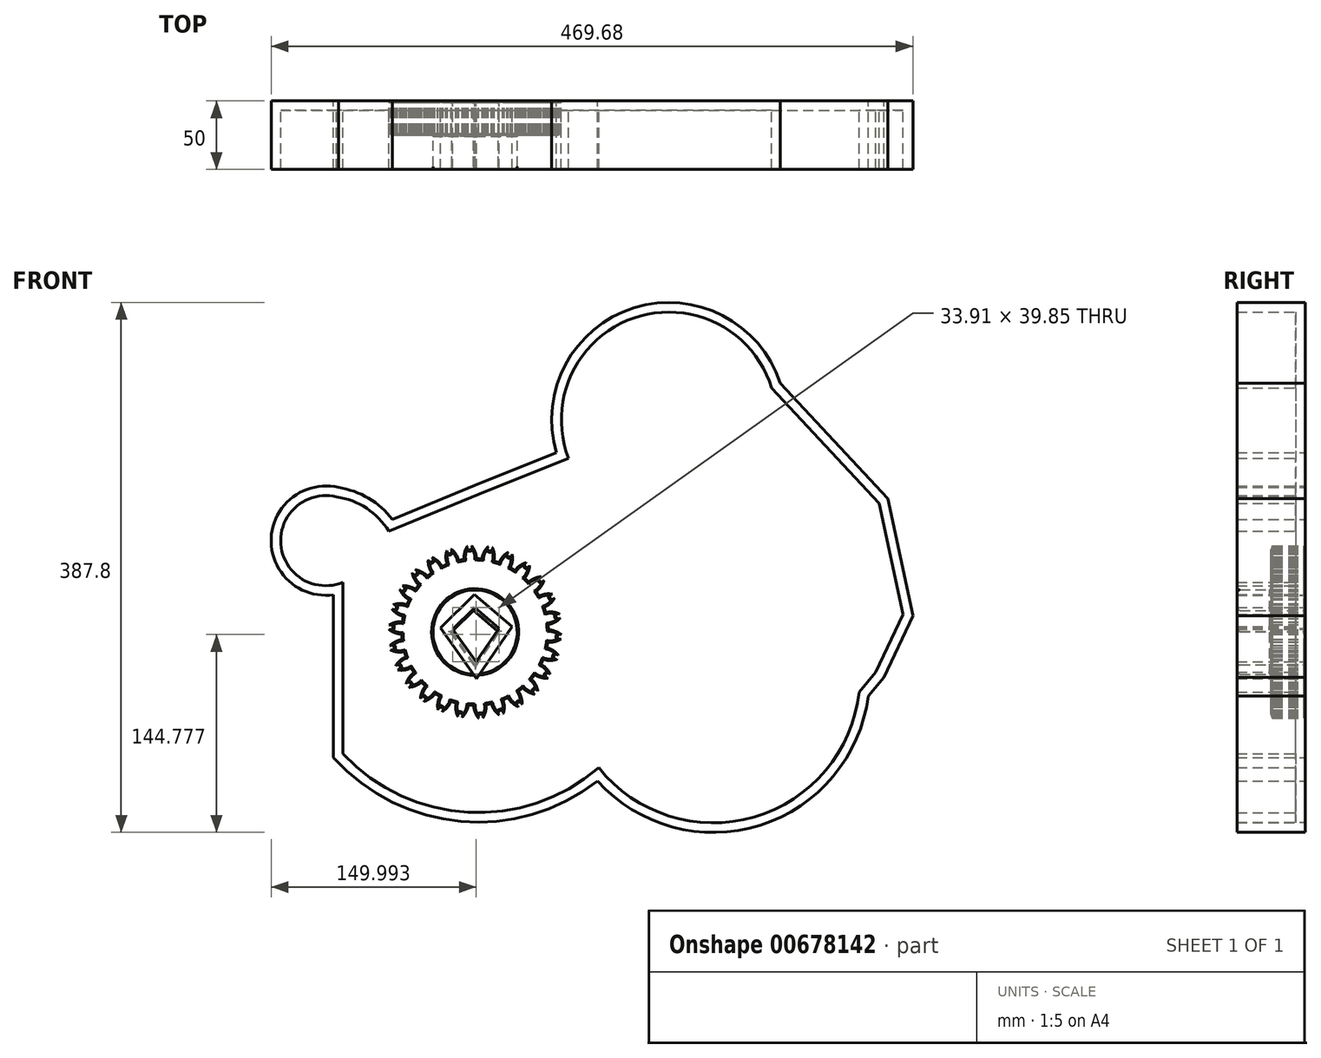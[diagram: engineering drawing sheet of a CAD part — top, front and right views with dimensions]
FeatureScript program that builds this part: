
annotation { "Feature Type Name" : "Feature", "Feature Type Description" : "" }
export const myFeature = defineFeature(function(context is Context, id is Id, definition is map)
    precondition{}
    {
        {
            var Q0;
            Q0=qCreatedBy(makeId("Front.planeOp"),FACE);
            var sketch = newSketch(context, id + "F0", { "sketchPlane" : qUnion([Q0])});
            skCircle(sketch, "E0", {"center": v(0, 0) * mm, "radius": 53.72 * mm});
            skCircle(sketch, "E1", {"center": v(0, 0) * mm, "radius": 58.67 * mm, "construction": true});
            skCircle(sketch, "E2", {"center": v(0, 0) * mm, "radius": 63.5 * mm, "construction": true});
            skLineSegment(sketch, "E3", {"start": v(0, 0) * mm, "end": v(0, 86.26) * mm, "construction": true});
            skLineSegment(sketch, "E4", {"start": v(0, 0) * mm, "end": v(-5.65, 86.26) * mm, "construction": true});
            skLineSegment(sketch, "E5", {"start": v(0, 58.67) * mm, "end": v(-58.15, 58.67) * mm, "construction": true});
            skLineSegment(sketch, "E6", {"start": v(0, 58.67) * mm, "end": v(-58.26, 37.47) * mm, "construction": true});
            skCircle(sketch, "E7", {"center": v(0, 0) * mm, "radius": 55.14 * mm, "construction": true});
            skCircle(sketch, "E8", {"center": v(0, 58.67) * mm, "radius": 14.6 * mm, "construction": true});
            skCircle(sketch, "E9", {"center": v(-13.72, 53.68) * mm, "radius": 14.6 * mm, "construction": true});
            skArc(sketch, "E10", {"start": v(0, 58.67) * mm, "mid": v(-1.18, 61.2) * mm, "end": v(-2.86, 63.44) * mm});
            skArc(sketch, "E11", {"start": v(0.88, 53.71) * mm, "mid": v(0.7, 56.24) * mm, "end": v(0, 58.67) * mm});
            skArc(sketch, "E12.MirrorCS", {"start": v(-7.66, 58.17) * mm, "mid": v(-6.82, 60.83) * mm, "end": v(-5.45, 63.27) * mm});
            skArc(sketch, "E13.MirrorCS", {"start": v(-7.88, 53.14) * mm, "mid": v(-8.04, 55.67) * mm, "end": v(-7.66, 58.17) * mm});
            skArc(sketch, "E14", {"start": v(-5.45, 63.27) * mm, "mid": v(-3.94, 60.17) * mm, "end": v(-2.86, 63.44) * mm});
            skCircle(sketch, "E15", {"center": v(0, 0) * mm, "radius": 30.81 * mm});
            skLineSegment(sketch, "E16", {"start": v(0, -24) * mm, "end": v(-17.1, 0) * mm});
            skLineSegment(sketch, "E17", {"start": v(-17.1, 0) * mm, "end": v(-1.04, 15.85) * mm});
            skLineSegment(sketch, "E18", {"start": v(-1.04, 15.85) * mm, "end": v(16.81, 0.43) * mm});
            skLineSegment(sketch, "E19", {"start": v(16.81, 0.43) * mm, "end": v(0, -24) * mm});
            skCircle(sketch, "E20", {"center": v(121.02, 0) * mm, "radius": 6 * mm});
            skSolve(sketch);
        }
        {
            var Q0;
            {var subQ0=sQuery(id+"F0.wireOp",EDGE,"E0");var subQ1=makeQuery(id+"F0.imprint","INTERSECT",VERTEX,{"derivedFrom":[subQ0,sQuery(id+"F0.wireOp",EDGE,"E11")]});Q0=makeQuery(id+"F0.imprint","IMPRINT",FACE,{"disambiguationData":[TD([[makeQuery(id+"F0.imprint","IMPRINT",EDGE,{"disambiguationData":[TD([[subQ1,-1.0]])],"derivedFrom":subQ0}),1.0]])]});}
            var Q1;
            {var subQ0=sQuery(id+"F0.wireOp",EDGE,"E11");Q1=makeQuery(id+"F0.imprint","IMPRINT",FACE,{"disambiguationData":[TD([[makeQuery(id+"F0.imprint","IMPRINT",EDGE,{"derivedFrom":subQ0}),1.0]])]});}
            extrude(context, id + "F1", {"entities" : qUnion([Q0, Q1]), "depth" : 25 * mm, "offsetDistance" : 25 * mm});
        }
        {
            var Q0;
            Q0=makeQuery(id+"F1.opExtrude","SWEPT_BODY",BODY,{"disambiguationData":[OSD([sQuery(id+"F0.wireOp",EDGE,"E0"),sQuery(id+"F0.wireOp",EDGE,"E10"),sQuery(id+"F0.wireOp",EDGE,"E11"),sQuery(id+"F0.wireOp",EDGE,"E12.MirrorCS"),sQuery(id+"F0.wireOp",EDGE,"E13.MirrorCS"),sQuery(id+"F0.wireOp",EDGE,"E14")])]});
            var Q1;
            Q1=makeQuery(id+"F1.opExtrude","SWEPT_FACE",FACE,{"disambiguationData":[OSD([sQuery(id+"F0.wireOp",EDGE,"E0")])]});
            circularPattern(context, id + "F2", {"entities" : qUnion([Q0]), "axis" : qUnion([Q1]), "angle" : 360 * degree, "instanceCount" : 26, "equalSpace" : true});
        }
        {
            var Q0;
            Q0=makeQuery(id+"F0.imprint","IMPRINT",FACE,{"disambiguationData":[TD([[makeQuery(id+"F0.imprint","IMPRINT",EDGE,{"derivedFrom":sQuery(id+"F0.wireOp",EDGE,"E15")}),1.0]])]});
            extrude(context, id + "F3", {"entities" : qUnion([Q0]), "operationType" : NewBodyOperationType.ADD, "depth" : 50 * mm, "offsetDistance" : 25 * mm});
        }
        {
            var Q0;
            {var subQ0=makeQuery(id+"F1.opExtrude","CAP_FACE",FACE,{"disambiguationData":[OSD([sQuery(id+"F0.wireOp",EDGE,"E0"),sQuery(id+"F0.wireOp",EDGE,"E10"),sQuery(id+"F0.wireOp",EDGE,"E11"),sQuery(id+"F0.wireOp",EDGE,"E12.MirrorCS"),sQuery(id+"F0.wireOp",EDGE,"E13.MirrorCS"),sQuery(id+"F0.wireOp",EDGE,"E14"),sQuery(id+"F0.wireOp",EDGE,"E15")])],"isStart":false});Q0=makeQuery(id+"F3.boolean.opBoolean","MERGE",FACE,{"derivedFrom":[subQ0,makeQuery(id+"F2.opPattern","COPY",FACE,{"derivedFrom":subQ0,"instanceName":"1"}),makeQuery(id+"F2.opPattern","COPY",FACE,{"derivedFrom":subQ0,"instanceName":"2"}),makeQuery(id+"F2.opPattern","COPY",FACE,{"derivedFrom":subQ0,"instanceName":"3"}),makeQuery(id+"F2.opPattern","COPY",FACE,{"derivedFrom":subQ0,"instanceName":"4"}),makeQuery(id+"F2.opPattern","COPY",FACE,{"derivedFrom":subQ0,"instanceName":"5"}),makeQuery(id+"F2.opPattern","COPY",FACE,{"derivedFrom":subQ0,"instanceName":"6"}),makeQuery(id+"F2.opPattern","COPY",FACE,{"derivedFrom":subQ0,"instanceName":"7"}),makeQuery(id+"F2.opPattern","COPY",FACE,{"derivedFrom":subQ0,"instanceName":"8"}),makeQuery(id+"F2.opPattern","COPY",FACE,{"derivedFrom":subQ0,"instanceName":"9"}),makeQuery(id+"F2.opPattern","COPY",FACE,{"derivedFrom":subQ0,"instanceName":"10"}),makeQuery(id+"F2.opPattern","COPY",FACE,{"derivedFrom":subQ0,"instanceName":"11"}),makeQuery(id+"F2.opPattern","COPY",FACE,{"derivedFrom":subQ0,"instanceName":"12"}),makeQuery(id+"F2.opPattern","COPY",FACE,{"derivedFrom":subQ0,"instanceName":"13"}),makeQuery(id+"F2.opPattern","COPY",FACE,{"derivedFrom":subQ0,"instanceName":"14"}),makeQuery(id+"F2.opPattern","COPY",FACE,{"derivedFrom":subQ0,"instanceName":"15"}),makeQuery(id+"F2.opPattern","COPY",FACE,{"derivedFrom":subQ0,"instanceName":"16"}),makeQuery(id+"F2.opPattern","COPY",FACE,{"derivedFrom":subQ0,"instanceName":"17"}),makeQuery(id+"F2.opPattern","COPY",FACE,{"derivedFrom":subQ0,"instanceName":"18"}),makeQuery(id+"F2.opPattern","COPY",FACE,{"derivedFrom":subQ0,"instanceName":"19"}),makeQuery(id+"F2.opPattern","COPY",FACE,{"derivedFrom":subQ0,"instanceName":"20"}),makeQuery(id+"F2.opPattern","COPY",FACE,{"derivedFrom":subQ0,"instanceName":"21"}),makeQuery(id+"F2.opPattern","COPY",FACE,{"derivedFrom":subQ0,"instanceName":"22"}),makeQuery(id+"F2.opPattern","COPY",FACE,{"derivedFrom":subQ0,"instanceName":"23"}),makeQuery(id+"F2.opPattern","COPY",FACE,{"derivedFrom":subQ0,"instanceName":"24"}),makeQuery(id+"F2.opPattern","COPY",FACE,{"derivedFrom":subQ0,"instanceName":"25"})]});}
            chamfer(context, id + "F4", {"entities" : qUnion([Q0]), "width" : 1 * mm, "tangentPropagation" : true});
        }
        {
            var Q0;
            {var subQ0=sQuery(id+"F0.wireOp",EDGE,"E15");var subQ1=makeQuery(id+"F1.opExtrude","CAP_FACE",FACE,{"disambiguationData":[OSD([sQuery(id+"F0.wireOp",EDGE,"E0"),sQuery(id+"F0.wireOp",EDGE,"E10"),sQuery(id+"F0.wireOp",EDGE,"E11"),sQuery(id+"F0.wireOp",EDGE,"E12.MirrorCS"),sQuery(id+"F0.wireOp",EDGE,"E13.MirrorCS"),sQuery(id+"F0.wireOp",EDGE,"E14"),subQ0])],"isStart":true});Q0=makeQuery(id+"F3.boolean.opBoolean","MERGE",FACE,{"derivedFrom":[subQ1,makeQuery(id+"F2.opPattern","COPY",FACE,{"derivedFrom":subQ1,"instanceName":"1"}),makeQuery(id+"F2.opPattern","COPY",FACE,{"derivedFrom":subQ1,"instanceName":"2"}),makeQuery(id+"F2.opPattern","COPY",FACE,{"derivedFrom":subQ1,"instanceName":"3"}),makeQuery(id+"F2.opPattern","COPY",FACE,{"derivedFrom":subQ1,"instanceName":"4"}),makeQuery(id+"F2.opPattern","COPY",FACE,{"derivedFrom":subQ1,"instanceName":"5"}),makeQuery(id+"F2.opPattern","COPY",FACE,{"derivedFrom":subQ1,"instanceName":"6"}),makeQuery(id+"F2.opPattern","COPY",FACE,{"derivedFrom":subQ1,"instanceName":"7"}),makeQuery(id+"F2.opPattern","COPY",FACE,{"derivedFrom":subQ1,"instanceName":"8"}),makeQuery(id+"F2.opPattern","COPY",FACE,{"derivedFrom":subQ1,"instanceName":"9"}),makeQuery(id+"F2.opPattern","COPY",FACE,{"derivedFrom":subQ1,"instanceName":"10"}),makeQuery(id+"F2.opPattern","COPY",FACE,{"derivedFrom":subQ1,"instanceName":"11"}),makeQuery(id+"F2.opPattern","COPY",FACE,{"derivedFrom":subQ1,"instanceName":"12"}),makeQuery(id+"F2.opPattern","COPY",FACE,{"derivedFrom":subQ1,"instanceName":"13"}),makeQuery(id+"F2.opPattern","COPY",FACE,{"derivedFrom":subQ1,"instanceName":"14"}),makeQuery(id+"F2.opPattern","COPY",FACE,{"derivedFrom":subQ1,"instanceName":"15"}),makeQuery(id+"F2.opPattern","COPY",FACE,{"derivedFrom":subQ1,"instanceName":"16"}),makeQuery(id+"F2.opPattern","COPY",FACE,{"derivedFrom":subQ1,"instanceName":"17"}),makeQuery(id+"F2.opPattern","COPY",FACE,{"derivedFrom":subQ1,"instanceName":"18"}),makeQuery(id+"F2.opPattern","COPY",FACE,{"derivedFrom":subQ1,"instanceName":"19"}),makeQuery(id+"F2.opPattern","COPY",FACE,{"derivedFrom":subQ1,"instanceName":"20"}),makeQuery(id+"F2.opPattern","COPY",FACE,{"derivedFrom":subQ1,"instanceName":"21"}),makeQuery(id+"F2.opPattern","COPY",FACE,{"derivedFrom":subQ1,"instanceName":"22"}),makeQuery(id+"F2.opPattern","COPY",FACE,{"derivedFrom":subQ1,"instanceName":"23"}),makeQuery(id+"F2.opPattern","COPY",FACE,{"derivedFrom":subQ1,"instanceName":"24"}),makeQuery(id+"F2.opPattern","COPY",FACE,{"derivedFrom":subQ1,"instanceName":"25"}),makeQuery(id+"F3.opExtrude","CAP_FACE",FACE,{"disambiguationData":[OSD([subQ0,sQuery(id+"F0.wireOp",EDGE,"E16"),sQuery(id+"F0.wireOp",EDGE,"E17"),sQuery(id+"F0.wireOp",EDGE,"E18"),sQuery(id+"F0.wireOp",EDGE,"E19")])],"isStart":true})]});}
            chamfer(context, id + "F5", {"entities" : qUnion([Q0]), "width" : 1 * mm, "tangentPropagation" : true});
        }
        {
            var Q0;
            Q0=makeQuery(id+"F3.opExtrude","CAP_FACE",FACE,{"disambiguationData":[OSD([sQuery(id+"F0.wireOp",EDGE,"E15"),sQuery(id+"F0.wireOp",EDGE,"E16"),sQuery(id+"F0.wireOp",EDGE,"E17"),sQuery(id+"F0.wireOp",EDGE,"E18"),sQuery(id+"F0.wireOp",EDGE,"E19")])],"isStart":false});
            fillet(context, id + "F6", {"entities" : qUnion([Q0]), "radius" : 2 * mm, "tangentPropagation" : true, "allowEdgeOverflow" : false});
        }
        {
            var Q0;
            Q0=qCreatedBy(makeId("Front.planeOp"),FACE);
            var sketch = newSketch(context, id + "F7", { "sketchPlane" : qUnion([Q0])});
            skArc(sketch, "E21", {"start": v(-103.62, -91.89) * mm, "mid": v(-10.38, -138.6) * mm, "end": v(89.64, -109.08) * mm});
            skLineSegment(sketch, "E22", {"start": v(-103.62, -91.89) * mm, "end": v(-103.62, 27.29) * mm});
            skArc(sketch, "E23", {"start": v(-99.97, 105.78) * mm, "mid": v(-149.22, 68.74) * mm, "end": v(-103.62, 27.29) * mm});
            skArc(sketch, "E24", {"start": v(-60.46, 82.38) * mm, "mid": v(-77.94, 97.92) * mm, "end": v(-99.97, 105.78) * mm});
            skLineSegment(sketch, "E25", {"start": v(-60.46, 82.38) * mm, "end": v(0, 107.34) * mm});
            skLineSegment(sketch, "E26", {"start": v(0, 107.34) * mm, "end": v(59.61, 131.25) * mm});
            skArc(sketch, "E27", {"start": v(223.25, 182.17) * mm, "mid": v(116.36, 237.28) * mm, "end": v(59.61, 131.25) * mm});
            skLineSegment(sketch, "E28", {"start": v(223.25, 182.17) * mm, "end": v(302.14, 97.5) * mm});
            skLineSegment(sketch, "E29", {"start": v(302.14, 97.5) * mm, "end": v(320.42, 11.88) * mm});
            skLineSegment(sketch, "E30", {"start": v(320.42, 11.88) * mm, "end": v(299.25, -33.34) * mm});
            skLineSegment(sketch, "E31", {"start": v(299.25, -33.34) * mm, "end": v(287.7, -46.8) * mm});
            skArc(sketch, "E32", {"start": v(89.64, -109.08) * mm, "mid": v(208.62, -141.4) * mm, "end": v(287.7, -46.8) * mm});
            skLineSegment(sketch, "E33", {"start": v(0.88, -21.8) * mm, "end": v(-16.22, 2.2) * mm});
            skLineSegment(sketch, "E34", {"start": v(-16.22, 2.2) * mm, "end": v(-0.16, 18.05) * mm});
            skLineSegment(sketch, "E35", {"start": v(-0.16, 18.05) * mm, "end": v(17.7, 2.63) * mm});
            skLineSegment(sketch, "E36", {"start": v(17.7, 2.63) * mm, "end": v(0.88, -21.8) * mm});
            skSolve(sketch);
        }
        {
            var Q0;
            Q0=makeQuery(id+"F7.imprint","IMPRINT",FACE,{"disambiguationData":[TD([[makeQuery(id+"F7.imprint","IMPRINT",EDGE,{"derivedFrom":sQuery(id+"F7.wireOp",EDGE,"E21")}),1.0]])]});
            extrude(context, id + "F8", {"entities" : qUnion([Q0]), "depth" : 50 * mm, "offsetDistance" : 25 * mm});
        }
        {
            var Q0;
            Q0=makeQuery(id+"F8.opExtrude","CAP_FACE",FACE,{"disambiguationData":[OSD([sQuery(id+"F7.wireOp",EDGE,"E21"),sQuery(id+"F7.wireOp",EDGE,"E22"),sQuery(id+"F7.wireOp",EDGE,"E23"),sQuery(id+"F7.wireOp",EDGE,"E24"),sQuery(id+"F7.wireOp",EDGE,"E25"),sQuery(id+"F7.wireOp",EDGE,"E26"),sQuery(id+"F7.wireOp",EDGE,"E27"),sQuery(id+"F7.wireOp",EDGE,"E28"),sQuery(id+"F7.wireOp",EDGE,"E29"),sQuery(id+"F7.wireOp",EDGE,"E30"),sQuery(id+"F7.wireOp",EDGE,"E31"),sQuery(id+"F7.wireOp",EDGE,"E32")])],"isStart":false});
            shell(context, id + "F9", {"entities" : qUnion([Q0]), "thickness" : 7 * mm});
        }
        {
            var Q0;
            Q0=sQuery(id+"F0.wireOp",EDGE,"E20");
            extrude(context, id + "F10", {"bodyType" : ToolBodyType.SURFACE, "surfaceEntities" : qUnion([Q0]), "depth" : 30 * mm, "offsetDistance" : 25 * mm});
        }
    });
